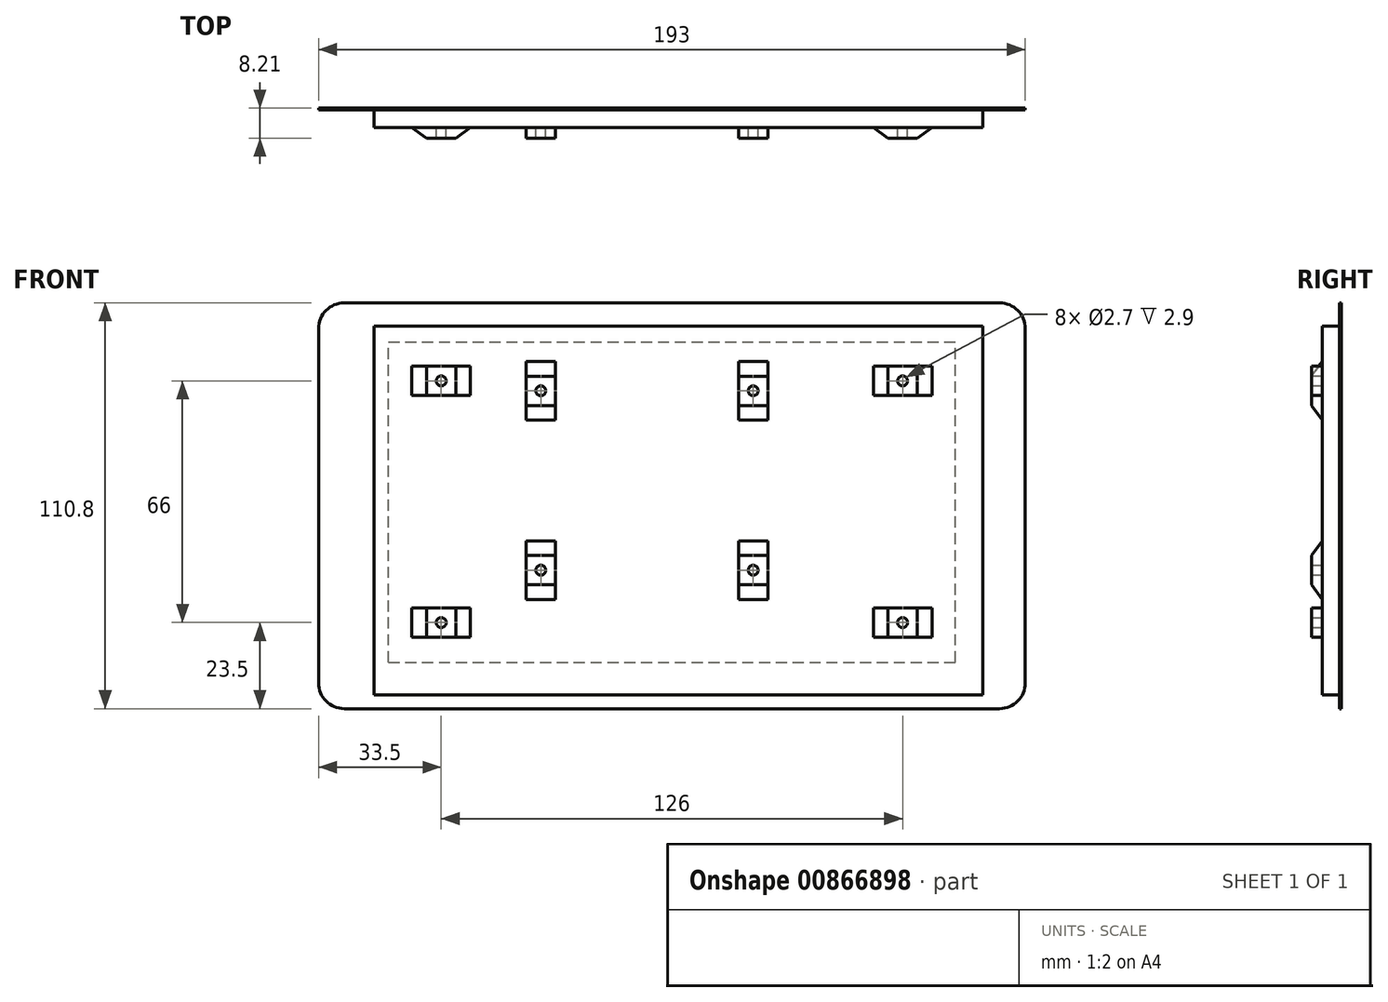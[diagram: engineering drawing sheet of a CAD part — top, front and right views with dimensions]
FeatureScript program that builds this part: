
annotation { "Feature Type Name" : "Feature", "Feature Type Description" : "" }
export const myFeature = defineFeature(function(context is Context, id is Id, definition is map)
    precondition{}
    {
        {
            var Q0;
            Q0=qCreatedBy(makeId("Front.planeOp"),FACE);
            var sketch = newSketch(context, id + "F0", { "sketchPlane" : qUnion([Q0])});
            skLineSegment(sketch, "E0.bottom", {"start": v(-111.7, 73) * mm, "end": v(67.3, 73) * mm});
            skLineSegment(sketch, "E0.top", {"start": v(-111.7, -37.8) * mm, "end": v(67.3, -37.8) * mm});
            skLineSegment(sketch, "E0.left", {"start": v(-118.7, 66) * mm, "end": v(-118.7, -30.8) * mm});
            skLineSegment(sketch, "E0.right", {"start": v(74.3, 66) * mm, "end": v(74.3, -30.8) * mm});
            skPoint(sketch, "E1.visualSharp", {"position": v(-118.7, 73) * mm});
            skArc(sketch, "E1.filletArc", {"start": v(-111.7, 73) * mm, "mid": v(-116.65, 70.95) * mm, "end": v(-118.7, 66) * mm});
            skPoint(sketch, "E2.visualSharp", {"position": v(-118.7, -37.8) * mm});
            skArc(sketch, "E2.filletArc", {"start": v(-118.7, -30.8) * mm, "mid": v(-116.65, -35.75) * mm, "end": v(-111.7, -37.8) * mm});
            skPoint(sketch, "E3.visualSharp", {"position": v(74.3, -37.8) * mm});
            skArc(sketch, "E3.filletArc", {"start": v(67.3, -37.8) * mm, "mid": v(72.25, -35.75) * mm, "end": v(74.3, -30.8) * mm});
            skPoint(sketch, "E4.visualSharp", {"position": v(74.3, 73) * mm});
            skArc(sketch, "E4.filletArc", {"start": v(74.3, 66) * mm, "mid": v(72.25, 70.95) * mm, "end": v(67.3, 73) * mm});
            skCircle(sketch, "E5", {"center": v(-58, 49) * mm, "radius": 1.35 * mm});
            skCircle(sketch, "E6", {"center": v(0, 49) * mm, "radius": 1.35 * mm});
            skCircle(sketch, "E7", {"center": v(-58, 0) * mm, "radius": 1.35 * mm});
            skCircle(sketch, "E8", {"center": v(0, 0) * mm, "radius": 1.35 * mm});
            skCircle(sketch, "E9", {"center": v(-85.2, 51.7) * mm, "radius": 1.35 * mm});
            skCircle(sketch, "E10", {"center": v(40.8, 51.7) * mm, "radius": 1.35 * mm});
            skCircle(sketch, "E11", {"center": v(40.8, -14.3) * mm, "radius": 1.35 * mm});
            skCircle(sketch, "E12", {"center": v(-85.2, -14.3) * mm, "radius": 1.35 * mm});
            skLineSegment(sketch, "E13", {"start": v(-85.2, -14.3) * mm, "end": v(-118.7, -14.3) * mm, "construction": true});
            skLineSegment(sketch, "E14", {"start": v(40.8, -14.3) * mm, "end": v(74.3, -14.3) * mm, "construction": true});
            skLineSegment(sketch, "E15.bottom", {"start": v(-103.6, 66.7) * mm, "end": v(62.7, 66.7) * mm});
            skLineSegment(sketch, "E15.top", {"start": v(-103.6, -34) * mm, "end": v(62.7, -34) * mm});
            skLineSegment(sketch, "E15.left", {"start": v(-103.6, 66.7) * mm, "end": v(-103.6, -34) * mm});
            skLineSegment(sketch, "E15.right", {"start": v(62.7, 66.7) * mm, "end": v(62.7, -34) * mm});
            skLineSegment(sketch, "E16.bottom", {"start": v(-54, 45) * mm, "end": v(-62, 45) * mm});
            skLineSegment(sketch, "E16.top", {"start": v(-54, 53) * mm, "end": v(-62, 53) * mm});
            skLineSegment(sketch, "E16.left", {"start": v(-54, 45) * mm, "end": v(-54, 53) * mm});
            skLineSegment(sketch, "E16.right", {"start": v(-62, 45) * mm, "end": v(-62, 53) * mm});
            skLineSegment(sketch, "E17.bottom", {"start": v(4, 45) * mm, "end": v(-4, 45) * mm});
            skLineSegment(sketch, "E17.top", {"start": v(4, 53) * mm, "end": v(-4, 53) * mm});
            skLineSegment(sketch, "E17.left", {"start": v(4, 45) * mm, "end": v(4, 53) * mm});
            skLineSegment(sketch, "E17.right", {"start": v(-4, 45) * mm, "end": v(-4, 53) * mm});
            skLineSegment(sketch, "E18.bottom", {"start": v(4, -4) * mm, "end": v(-4, -4) * mm});
            skLineSegment(sketch, "E18.top", {"start": v(4, 4) * mm, "end": v(-4, 4) * mm});
            skLineSegment(sketch, "E18.left", {"start": v(4, -4) * mm, "end": v(4, 4) * mm});
            skLineSegment(sketch, "E18.right", {"start": v(-4, -4) * mm, "end": v(-4, 4) * mm});
            skLineSegment(sketch, "E19.bottom", {"start": v(-54, -4) * mm, "end": v(-62, -4) * mm});
            skLineSegment(sketch, "E19.top", {"start": v(-54, 4) * mm, "end": v(-62, 4) * mm});
            skLineSegment(sketch, "E19.left", {"start": v(-54, -4) * mm, "end": v(-54, 4) * mm});
            skLineSegment(sketch, "E19.right", {"start": v(-62, -4) * mm, "end": v(-62, 4) * mm});
            skLineSegment(sketch, "E20.bottom", {"start": v(-81.2, -18.3) * mm, "end": v(-89.2, -18.3) * mm});
            skLineSegment(sketch, "E20.top", {"start": v(-81.2, -10.3) * mm, "end": v(-89.2, -10.3) * mm});
            skLineSegment(sketch, "E20.left", {"start": v(-81.2, -18.3) * mm, "end": v(-81.2, -10.3) * mm});
            skLineSegment(sketch, "E20.right", {"start": v(-89.2, -18.3) * mm, "end": v(-89.2, -10.3) * mm});
            skLineSegment(sketch, "E21.bottom", {"start": v(-81.2, 47.7) * mm, "end": v(-89.2, 47.7) * mm});
            skLineSegment(sketch, "E21.top", {"start": v(-81.2, 55.7) * mm, "end": v(-89.2, 55.7) * mm});
            skLineSegment(sketch, "E21.left", {"start": v(-81.2, 47.7) * mm, "end": v(-81.2, 55.7) * mm});
            skLineSegment(sketch, "E21.right", {"start": v(-89.2, 47.7) * mm, "end": v(-89.2, 55.7) * mm});
            skLineSegment(sketch, "E22.bottom", {"start": v(44.8, 47.7) * mm, "end": v(36.8, 47.7) * mm});
            skLineSegment(sketch, "E22.top", {"start": v(44.8, 55.7) * mm, "end": v(36.8, 55.7) * mm});
            skLineSegment(sketch, "E22.left", {"start": v(44.8, 47.7) * mm, "end": v(44.8, 55.7) * mm});
            skLineSegment(sketch, "E22.right", {"start": v(36.8, 47.7) * mm, "end": v(36.8, 55.7) * mm});
            skLineSegment(sketch, "E23.bottom", {"start": v(44.8, -18.3) * mm, "end": v(36.8, -18.3) * mm});
            skLineSegment(sketch, "E23.top", {"start": v(44.8, -10.3) * mm, "end": v(36.8, -10.3) * mm});
            skLineSegment(sketch, "E23.left", {"start": v(44.8, -18.3) * mm, "end": v(44.8, -10.3) * mm});
            skLineSegment(sketch, "E23.right", {"start": v(36.8, -18.3) * mm, "end": v(36.8, -10.3) * mm});
            skLineSegment(sketch, "E24.bottom", {"start": v(-99.6, -25.1) * mm, "end": v(55.2, -25.1) * mm});
            skLineSegment(sketch, "E24.top", {"start": v(-99.6, 62.3) * mm, "end": v(55.2, 62.3) * mm});
            skLineSegment(sketch, "E24.left", {"start": v(-99.6, -25.1) * mm, "end": v(-99.6, 62.3) * mm});
            skLineSegment(sketch, "E24.right", {"start": v(55.2, -25.1) * mm, "end": v(55.2, 62.3) * mm});
            skPoint(sketch, "E24.middle", {"position": v(-22.2, 18.6) * mm});
            skLineSegment(sketch, "E25", {"start": v(55.2, 18.6) * mm, "end": v(74.3, 18.6) * mm, "construction": true});
            skPoint(sketch, "E25.endSnap0", {"position": v(74.3, 17.6) * mm});
            skLineSegment(sketch, "E26", {"start": v(-99.6, 18.6) * mm, "end": v(-118.7, 18.6) * mm, "construction": true});
            skSolve(sketch);
        }
        {
            var Q0;
            Q0=makeQuery(id+"F0.imprint","IMPRINT",FACE,{"disambiguationData":[TD([[makeQuery(id+"F0.imprint","IMPRINT",EDGE,{"derivedFrom":sQuery(id+"F0.wireOp",EDGE,"E15.bottom")}),-1.0]])]});
            var Q1;
            Q1=makeQuery(id+"F0.imprint","IMPRINT",FACE,{"disambiguationData":[TD([[makeQuery(id+"F0.imprint","IMPRINT",EDGE,{"derivedFrom":sQuery(id+"F0.wireOp",EDGE,"E5")}),-1.0]])]});
            var Q2;
            Q2=makeQuery(id+"F0.imprint","IMPRINT",FACE,{"disambiguationData":[TD([[makeQuery(id+"F0.imprint","IMPRINT",EDGE,{"derivedFrom":sQuery(id+"F0.wireOp",EDGE,"E9")}),-1.0]])]});
            var Q3;
            Q3=makeQuery(id+"F0.imprint","IMPRINT",FACE,{"disambiguationData":[TD([[makeQuery(id+"F0.imprint","IMPRINT",EDGE,{"derivedFrom":sQuery(id+"F0.wireOp",EDGE,"E6")}),1.0]])]});
            var Q4;
            Q4=makeQuery(id+"F0.imprint","IMPRINT",FACE,{"disambiguationData":[TD([[makeQuery(id+"F0.imprint","IMPRINT",EDGE,{"derivedFrom":sQuery(id+"F0.wireOp",EDGE,"E10")}),-1.0]])]});
            var Q5;
            Q5=makeQuery(id+"F0.imprint","IMPRINT",FACE,{"disambiguationData":[TD([[makeQuery(id+"F0.imprint","IMPRINT",EDGE,{"derivedFrom":sQuery(id+"F0.wireOp",EDGE,"E8")}),-1.0]])]});
            var Q6;
            Q6=makeQuery(id+"F0.imprint","IMPRINT",FACE,{"disambiguationData":[TD([[makeQuery(id+"F0.imprint","IMPRINT",EDGE,{"derivedFrom":sQuery(id+"F0.wireOp",EDGE,"E11")}),-1.0]])]});
            var Q7;
            Q7=makeQuery(id+"F0.imprint","IMPRINT",FACE,{"disambiguationData":[TD([[makeQuery(id+"F0.imprint","IMPRINT",EDGE,{"derivedFrom":sQuery(id+"F0.wireOp",EDGE,"E6")}),-1.0]])]});
            var Q8;
            Q8=makeQuery(id+"F0.imprint","IMPRINT",FACE,{"disambiguationData":[TD([[makeQuery(id+"F0.imprint","IMPRINT",EDGE,{"derivedFrom":sQuery(id+"F0.wireOp",EDGE,"E10")}),1.0]])]});
            var Q9;
            Q9=makeQuery(id+"F0.imprint","IMPRINT",FACE,{"disambiguationData":[TD([[makeQuery(id+"F0.imprint","IMPRINT",EDGE,{"derivedFrom":sQuery(id+"F0.wireOp",EDGE,"E11")}),1.0]])]});
            var Q10;
            Q10=makeQuery(id+"F0.imprint","IMPRINT",FACE,{"disambiguationData":[TD([[makeQuery(id+"F0.imprint","IMPRINT",EDGE,{"derivedFrom":sQuery(id+"F0.wireOp",EDGE,"E8")}),1.0]])]});
            var Q11;
            Q11=makeQuery(id+"F0.imprint","IMPRINT",FACE,{"disambiguationData":[TD([[makeQuery(id+"F0.imprint","IMPRINT",EDGE,{"derivedFrom":sQuery(id+"F0.wireOp",EDGE,"E5")}),1.0]])]});
            var Q12;
            Q12=makeQuery(id+"F0.imprint","IMPRINT",FACE,{"disambiguationData":[TD([[makeQuery(id+"F0.imprint","IMPRINT",EDGE,{"derivedFrom":sQuery(id+"F0.wireOp",EDGE,"E7")}),1.0]])]});
            var Q13;
            Q13=makeQuery(id+"F0.imprint","IMPRINT",FACE,{"disambiguationData":[TD([[makeQuery(id+"F0.imprint","IMPRINT",EDGE,{"derivedFrom":sQuery(id+"F0.wireOp",EDGE,"E7")}),-1.0]])]});
            var Q14;
            Q14=makeQuery(id+"F0.imprint","IMPRINT",FACE,{"disambiguationData":[TD([[makeQuery(id+"F0.imprint","IMPRINT",EDGE,{"derivedFrom":sQuery(id+"F0.wireOp",EDGE,"E9")}),1.0]])]});
            var Q15;
            Q15=makeQuery(id+"F0.imprint","IMPRINT",FACE,{"disambiguationData":[TD([[makeQuery(id+"F0.imprint","IMPRINT",EDGE,{"derivedFrom":sQuery(id+"F0.wireOp",EDGE,"E12")}),1.0]])]});
            var Q16;
            Q16=makeQuery(id+"F0.imprint","IMPRINT",FACE,{"disambiguationData":[TD([[makeQuery(id+"F0.imprint","IMPRINT",EDGE,{"derivedFrom":sQuery(id+"F0.wireOp",EDGE,"E12")}),-1.0]])]});
            var Q17;
            Q17=makeQuery(id+"F0.imprint","IMPRINT",FACE,{"disambiguationData":[TD([[makeQuery(id+"F0.imprint","IMPRINT",EDGE,{"derivedFrom":sQuery(id+"F0.wireOp",EDGE,"E0.bottom")}),-1.0]])]});
            var Q18;
            Q18=makeQuery(id+"F0.imprint","IMPRINT",FACE,{"disambiguationData":[TD([[makeQuery(id+"F0.imprint","IMPRINT",EDGE,{"derivedFrom":sQuery(id+"F0.wireOp",EDGE,"E16.bottom")}),1.0]])]});
            var Q19;
            Q19=sQuery(id+"F0.wireOp",EDGE,"E0.bottom");
            var Q20;
            Q20=sQuery(id+"F0.wireOp",EDGE,"E1.filletArc");
            var Q21;
            Q21=sQuery(id+"F0.wireOp",EDGE,"E0.left");
            var Q22;
            Q22=sQuery(id+"F0.wireOp",EDGE,"E2.filletArc");
            var Q23;
            Q23=sQuery(id+"F0.wireOp",EDGE,"E0.top");
            var Q24;
            Q24=sQuery(id+"F0.wireOp",EDGE,"E3.filletArc");
            var Q25;
            Q25=sQuery(id+"F0.wireOp",EDGE,"E0.right");
            var Q26;
            Q26=sQuery(id+"F0.wireOp",EDGE,"E4.filletArc");
            extrude(context, id + "F1", {"entities" : qUnion([Q0, Q1, Q2, Q3, Q4, Q5, Q6, Q7, Q8, Q9, Q10, Q11, Q12, Q13, Q14, Q15, Q16, Q17, Q18]), "surfaceEntities" : qUnion([Q19, Q20, Q21, Q22, Q23, Q24, Q25, Q26]), "oppositeDirection" : true, "depth" : .5 * mm, "offsetDistance" : 25 * mm});
        }
        {
            var Q0;
            Q0=makeQuery(id+"F0.imprint","IMPRINT",FACE,{"disambiguationData":[TD([[makeQuery(id+"F0.imprint","IMPRINT",EDGE,{"derivedFrom":sQuery(id+"F0.wireOp",EDGE,"E15.bottom")}),-1.0]])]});
            var Q1;
            Q1=makeQuery(id+"F0.imprint","IMPRINT",FACE,{"disambiguationData":[TD([[makeQuery(id+"F0.imprint","IMPRINT",EDGE,{"derivedFrom":sQuery(id+"F0.wireOp",EDGE,"E10")}),-1.0]])]});
            var Q2;
            Q2=makeQuery(id+"F0.imprint","IMPRINT",FACE,{"disambiguationData":[TD([[makeQuery(id+"F0.imprint","IMPRINT",EDGE,{"derivedFrom":sQuery(id+"F0.wireOp",EDGE,"E10")}),1.0]])]});
            var Q3;
            Q3=makeQuery(id+"F0.imprint","IMPRINT",FACE,{"disambiguationData":[TD([[makeQuery(id+"F0.imprint","IMPRINT",EDGE,{"derivedFrom":sQuery(id+"F0.wireOp",EDGE,"E6")}),-1.0]])]});
            var Q4;
            Q4=makeQuery(id+"F0.imprint","IMPRINT",FACE,{"disambiguationData":[TD([[makeQuery(id+"F0.imprint","IMPRINT",EDGE,{"derivedFrom":sQuery(id+"F0.wireOp",EDGE,"E6")}),1.0]])]});
            var Q5;
            Q5=makeQuery(id+"F0.imprint","IMPRINT",FACE,{"disambiguationData":[TD([[makeQuery(id+"F0.imprint","IMPRINT",EDGE,{"derivedFrom":sQuery(id+"F0.wireOp",EDGE,"E5")}),-1.0]])]});
            var Q6;
            Q6=makeQuery(id+"F0.imprint","IMPRINT",FACE,{"disambiguationData":[TD([[makeQuery(id+"F0.imprint","IMPRINT",EDGE,{"derivedFrom":sQuery(id+"F0.wireOp",EDGE,"E5")}),1.0]])]});
            var Q7;
            Q7=makeQuery(id+"F0.imprint","IMPRINT",FACE,{"disambiguationData":[TD([[makeQuery(id+"F0.imprint","IMPRINT",EDGE,{"derivedFrom":sQuery(id+"F0.wireOp",EDGE,"E9")}),-1.0]])]});
            var Q8;
            Q8=makeQuery(id+"F0.imprint","IMPRINT",FACE,{"disambiguationData":[TD([[makeQuery(id+"F0.imprint","IMPRINT",EDGE,{"derivedFrom":sQuery(id+"F0.wireOp",EDGE,"E9")}),1.0]])]});
            var Q9;
            Q9=makeQuery(id+"F0.imprint","IMPRINT",FACE,{"disambiguationData":[TD([[makeQuery(id+"F0.imprint","IMPRINT",EDGE,{"derivedFrom":sQuery(id+"F0.wireOp",EDGE,"E7")}),-1.0]])]});
            var Q10;
            Q10=makeQuery(id+"F0.imprint","IMPRINT",FACE,{"disambiguationData":[TD([[makeQuery(id+"F0.imprint","IMPRINT",EDGE,{"derivedFrom":sQuery(id+"F0.wireOp",EDGE,"E7")}),1.0]])]});
            var Q11;
            Q11=makeQuery(id+"F0.imprint","IMPRINT",FACE,{"disambiguationData":[TD([[makeQuery(id+"F0.imprint","IMPRINT",EDGE,{"derivedFrom":sQuery(id+"F0.wireOp",EDGE,"E12")}),-1.0]])]});
            var Q12;
            Q12=makeQuery(id+"F0.imprint","IMPRINT",FACE,{"disambiguationData":[TD([[makeQuery(id+"F0.imprint","IMPRINT",EDGE,{"derivedFrom":sQuery(id+"F0.wireOp",EDGE,"E12")}),1.0]])]});
            var Q13;
            Q13=makeQuery(id+"F0.imprint","IMPRINT",FACE,{"disambiguationData":[TD([[makeQuery(id+"F0.imprint","IMPRINT",EDGE,{"derivedFrom":sQuery(id+"F0.wireOp",EDGE,"E8")}),-1.0]])]});
            var Q14;
            Q14=makeQuery(id+"F0.imprint","IMPRINT",FACE,{"disambiguationData":[TD([[makeQuery(id+"F0.imprint","IMPRINT",EDGE,{"derivedFrom":sQuery(id+"F0.wireOp",EDGE,"E8")}),1.0]])]});
            var Q15;
            Q15=makeQuery(id+"F0.imprint","IMPRINT",FACE,{"disambiguationData":[TD([[makeQuery(id+"F0.imprint","IMPRINT",EDGE,{"derivedFrom":sQuery(id+"F0.wireOp",EDGE,"E11")}),-1.0]])]});
            var Q16;
            Q16=makeQuery(id+"F0.imprint","IMPRINT",FACE,{"disambiguationData":[TD([[makeQuery(id+"F0.imprint","IMPRINT",EDGE,{"derivedFrom":sQuery(id+"F0.wireOp",EDGE,"E11")}),1.0]])]});
            var Q17;
            Q17=makeQuery(id+"F0.imprint","IMPRINT",FACE,{"disambiguationData":[TD([[makeQuery(id+"F0.imprint","IMPRINT",EDGE,{"derivedFrom":sQuery(id+"F0.wireOp",EDGE,"E16.bottom")}),1.0]])]});
            extrude(context, id + "F2", {"entities" : qUnion([Q0, Q1, Q2, Q3, Q4, Q5, Q6, Q7, Q8, Q9, Q10, Q11, Q12, Q13, Q14, Q15, Q16, Q17]), "depth" : 4.8 * mm, "offsetDistance" : 25 * mm});
        }
        {
            var Q0;
            Q0=makeQuery(id+"F0.imprint","IMPRINT",FACE,{"disambiguationData":[TD([[makeQuery(id+"F0.imprint","IMPRINT",EDGE,{"derivedFrom":sQuery(id+"F0.wireOp",EDGE,"E5")}),-1.0]])]});
            var Q1;
            Q1=makeQuery(id+"F0.imprint","IMPRINT",FACE,{"disambiguationData":[TD([[makeQuery(id+"F0.imprint","IMPRINT",EDGE,{"derivedFrom":sQuery(id+"F0.wireOp",EDGE,"E6")}),-1.0]])]});
            var Q2;
            Q2=makeQuery(id+"F0.imprint","IMPRINT",FACE,{"disambiguationData":[TD([[makeQuery(id+"F0.imprint","IMPRINT",EDGE,{"derivedFrom":sQuery(id+"F0.wireOp",EDGE,"E10")}),-1.0]])]});
            var Q3;
            Q3=makeQuery(id+"F0.imprint","IMPRINT",FACE,{"disambiguationData":[TD([[makeQuery(id+"F0.imprint","IMPRINT",EDGE,{"derivedFrom":sQuery(id+"F0.wireOp",EDGE,"E11")}),-1.0]])]});
            var Q4;
            Q4=makeQuery(id+"F0.imprint","IMPRINT",FACE,{"disambiguationData":[TD([[makeQuery(id+"F0.imprint","IMPRINT",EDGE,{"derivedFrom":sQuery(id+"F0.wireOp",EDGE,"E8")}),-1.0]])]});
            var Q5;
            Q5=makeQuery(id+"F0.imprint","IMPRINT",FACE,{"disambiguationData":[TD([[makeQuery(id+"F0.imprint","IMPRINT",EDGE,{"derivedFrom":sQuery(id+"F0.wireOp",EDGE,"E7")}),-1.0]])]});
            var Q6;
            Q6=makeQuery(id+"F0.imprint","IMPRINT",FACE,{"disambiguationData":[TD([[makeQuery(id+"F0.imprint","IMPRINT",EDGE,{"derivedFrom":sQuery(id+"F0.wireOp",EDGE,"E12")}),-1.0]])]});
            var Q7;
            Q7=makeQuery(id+"F0.imprint","IMPRINT",FACE,{"disambiguationData":[TD([[makeQuery(id+"F0.imprint","IMPRINT",EDGE,{"derivedFrom":sQuery(id+"F0.wireOp",EDGE,"E9")}),-1.0]])]});
            extrude(context, id + "F3", {"entities" : qUnion([Q0, Q1, Q2, Q3, Q4, Q5, Q6, Q7]), "operationType" : NewBodyOperationType.ADD, "depth" : 7.7 * mm, "offsetDistance" : 25 * mm});
        }
        {
            var Q0;
            Q0=makeQuery(id+"F3.boolean.opBoolean","INTERSECT",EDGE,{"derivedFrom":[makeQuery(id+"F2.opExtrude","CAP_FACE",FACE,{"disambiguationData":[OSD([sQuery(id+"F0.wireOp",EDGE,"E15.bottom"),sQuery(id+"F0.wireOp",EDGE,"E15.top"),sQuery(id+"F0.wireOp",EDGE,"E15.left"),sQuery(id+"F0.wireOp",EDGE,"E15.right")])],"isStart":false}),makeQuery(id+"F3.opExtrude","SWEPT_FACE",FACE,{"disambiguationData":[OSD([sQuery(id+"F0.wireOp",EDGE,"E16.top")])]})]});
            var Q1;
            Q1=makeQuery(id+"F3.boolean.opBoolean","INTERSECT",EDGE,{"derivedFrom":[makeQuery(id+"F2.opExtrude","CAP_FACE",FACE,{"disambiguationData":[OSD([sQuery(id+"F0.wireOp",EDGE,"E15.bottom"),sQuery(id+"F0.wireOp",EDGE,"E15.top"),sQuery(id+"F0.wireOp",EDGE,"E15.left"),sQuery(id+"F0.wireOp",EDGE,"E15.right")])],"isStart":false}),makeQuery(id+"F3.opExtrude","SWEPT_FACE",FACE,{"disambiguationData":[OSD([sQuery(id+"F0.wireOp",EDGE,"E16.bottom")])]})]});
            var Q2;
            Q2=makeQuery(id+"F3.boolean.opBoolean","INTERSECT",EDGE,{"derivedFrom":[makeQuery(id+"F2.opExtrude","CAP_FACE",FACE,{"disambiguationData":[OSD([sQuery(id+"F0.wireOp",EDGE,"E15.bottom"),sQuery(id+"F0.wireOp",EDGE,"E15.top"),sQuery(id+"F0.wireOp",EDGE,"E15.left"),sQuery(id+"F0.wireOp",EDGE,"E15.right")])],"isStart":false}),makeQuery(id+"F3.opExtrude","SWEPT_FACE",FACE,{"disambiguationData":[OSD([sQuery(id+"F0.wireOp",EDGE,"E21.right")])]})]});
            var Q3;
            Q3=makeQuery(id+"F3.boolean.opBoolean","INTERSECT",EDGE,{"derivedFrom":[makeQuery(id+"F2.opExtrude","CAP_FACE",FACE,{"disambiguationData":[OSD([sQuery(id+"F0.wireOp",EDGE,"E15.bottom"),sQuery(id+"F0.wireOp",EDGE,"E15.top"),sQuery(id+"F0.wireOp",EDGE,"E15.left"),sQuery(id+"F0.wireOp",EDGE,"E15.right")])],"isStart":false}),makeQuery(id+"F3.opExtrude","SWEPT_FACE",FACE,{"disambiguationData":[OSD([sQuery(id+"F0.wireOp",EDGE,"E21.left")])]})]});
            var Q4;
            Q4=makeQuery(id+"F3.boolean.opBoolean","INTERSECT",EDGE,{"derivedFrom":[makeQuery(id+"F2.opExtrude","CAP_FACE",FACE,{"disambiguationData":[OSD([sQuery(id+"F0.wireOp",EDGE,"E15.bottom"),sQuery(id+"F0.wireOp",EDGE,"E15.top"),sQuery(id+"F0.wireOp",EDGE,"E15.left"),sQuery(id+"F0.wireOp",EDGE,"E15.right")])],"isStart":false}),makeQuery(id+"F3.opExtrude","SWEPT_FACE",FACE,{"disambiguationData":[OSD([sQuery(id+"F0.wireOp",EDGE,"E17.bottom")])]})]});
            var Q5;
            Q5=makeQuery(id+"F3.boolean.opBoolean","INTERSECT",EDGE,{"derivedFrom":[makeQuery(id+"F2.opExtrude","CAP_FACE",FACE,{"disambiguationData":[OSD([sQuery(id+"F0.wireOp",EDGE,"E15.bottom"),sQuery(id+"F0.wireOp",EDGE,"E15.top"),sQuery(id+"F0.wireOp",EDGE,"E15.left"),sQuery(id+"F0.wireOp",EDGE,"E15.right")])],"isStart":false}),makeQuery(id+"F3.opExtrude","SWEPT_FACE",FACE,{"disambiguationData":[OSD([sQuery(id+"F0.wireOp",EDGE,"E18.bottom")])]})]});
            var Q6;
            Q6=makeQuery(id+"F3.boolean.opBoolean","INTERSECT",EDGE,{"derivedFrom":[makeQuery(id+"F2.opExtrude","CAP_FACE",FACE,{"disambiguationData":[OSD([sQuery(id+"F0.wireOp",EDGE,"E15.bottom"),sQuery(id+"F0.wireOp",EDGE,"E15.top"),sQuery(id+"F0.wireOp",EDGE,"E15.left"),sQuery(id+"F0.wireOp",EDGE,"E15.right")])],"isStart":false}),makeQuery(id+"F3.opExtrude","SWEPT_FACE",FACE,{"disambiguationData":[OSD([sQuery(id+"F0.wireOp",EDGE,"E23.left")])]})]});
            var Q7;
            Q7=makeQuery(id+"F3.boolean.opBoolean","INTERSECT",EDGE,{"derivedFrom":[makeQuery(id+"F2.opExtrude","CAP_FACE",FACE,{"disambiguationData":[OSD([sQuery(id+"F0.wireOp",EDGE,"E15.bottom"),sQuery(id+"F0.wireOp",EDGE,"E15.top"),sQuery(id+"F0.wireOp",EDGE,"E15.left"),sQuery(id+"F0.wireOp",EDGE,"E15.right")])],"isStart":false}),makeQuery(id+"F3.opExtrude","SWEPT_FACE",FACE,{"disambiguationData":[OSD([sQuery(id+"F0.wireOp",EDGE,"E22.left")])]})]});
            var Q8;
            Q8=makeQuery(id+"F3.boolean.opBoolean","INTERSECT",EDGE,{"derivedFrom":[makeQuery(id+"F2.opExtrude","CAP_FACE",FACE,{"disambiguationData":[OSD([sQuery(id+"F0.wireOp",EDGE,"E15.bottom"),sQuery(id+"F0.wireOp",EDGE,"E15.top"),sQuery(id+"F0.wireOp",EDGE,"E15.left"),sQuery(id+"F0.wireOp",EDGE,"E15.right")])],"isStart":false}),makeQuery(id+"F3.opExtrude","SWEPT_FACE",FACE,{"disambiguationData":[OSD([sQuery(id+"F0.wireOp",EDGE,"E19.bottom")])]})]});
            var Q9;
            Q9=makeQuery(id+"F3.boolean.opBoolean","INTERSECT",EDGE,{"derivedFrom":[makeQuery(id+"F2.opExtrude","CAP_FACE",FACE,{"disambiguationData":[OSD([sQuery(id+"F0.wireOp",EDGE,"E15.bottom"),sQuery(id+"F0.wireOp",EDGE,"E15.top"),sQuery(id+"F0.wireOp",EDGE,"E15.left"),sQuery(id+"F0.wireOp",EDGE,"E15.right")])],"isStart":false}),makeQuery(id+"F3.opExtrude","SWEPT_FACE",FACE,{"disambiguationData":[OSD([sQuery(id+"F0.wireOp",EDGE,"E20.left")])]})]});
            var Q10;
            Q10=makeQuery(id+"F3.boolean.opBoolean","INTERSECT",EDGE,{"derivedFrom":[makeQuery(id+"F2.opExtrude","CAP_FACE",FACE,{"disambiguationData":[OSD([sQuery(id+"F0.wireOp",EDGE,"E15.bottom"),sQuery(id+"F0.wireOp",EDGE,"E15.top"),sQuery(id+"F0.wireOp",EDGE,"E15.left"),sQuery(id+"F0.wireOp",EDGE,"E15.right")])],"isStart":false}),makeQuery(id+"F3.opExtrude","SWEPT_FACE",FACE,{"disambiguationData":[OSD([sQuery(id+"F0.wireOp",EDGE,"E20.right")])]})]});
            var Q11;
            Q11=makeQuery(id+"F3.boolean.opBoolean","INTERSECT",EDGE,{"derivedFrom":[makeQuery(id+"F2.opExtrude","CAP_FACE",FACE,{"disambiguationData":[OSD([sQuery(id+"F0.wireOp",EDGE,"E15.bottom"),sQuery(id+"F0.wireOp",EDGE,"E15.top"),sQuery(id+"F0.wireOp",EDGE,"E15.left"),sQuery(id+"F0.wireOp",EDGE,"E15.right")])],"isStart":false}),makeQuery(id+"F3.opExtrude","SWEPT_FACE",FACE,{"disambiguationData":[OSD([sQuery(id+"F0.wireOp",EDGE,"E22.right")])]})]});
            var Q12;
            Q12=makeQuery(id+"F3.boolean.opBoolean","INTERSECT",EDGE,{"derivedFrom":[makeQuery(id+"F2.opExtrude","CAP_FACE",FACE,{"disambiguationData":[OSD([sQuery(id+"F0.wireOp",EDGE,"E15.bottom"),sQuery(id+"F0.wireOp",EDGE,"E15.top"),sQuery(id+"F0.wireOp",EDGE,"E15.left"),sQuery(id+"F0.wireOp",EDGE,"E15.right")])],"isStart":false}),makeQuery(id+"F3.opExtrude","SWEPT_FACE",FACE,{"disambiguationData":[OSD([sQuery(id+"F0.wireOp",EDGE,"E23.right")])]})]});
            var Q13;
            Q13=makeQuery(id+"F3.boolean.opBoolean","INTERSECT",EDGE,{"derivedFrom":[makeQuery(id+"F2.opExtrude","CAP_FACE",FACE,{"disambiguationData":[OSD([sQuery(id+"F0.wireOp",EDGE,"E15.bottom"),sQuery(id+"F0.wireOp",EDGE,"E15.top"),sQuery(id+"F0.wireOp",EDGE,"E15.left"),sQuery(id+"F0.wireOp",EDGE,"E15.right")])],"isStart":false}),makeQuery(id+"F3.opExtrude","SWEPT_FACE",FACE,{"disambiguationData":[OSD([sQuery(id+"F0.wireOp",EDGE,"E17.top")])]})]});
            var Q14;
            Q14=makeQuery(id+"F3.boolean.opBoolean","INTERSECT",EDGE,{"derivedFrom":[makeQuery(id+"F2.opExtrude","CAP_FACE",FACE,{"disambiguationData":[OSD([sQuery(id+"F0.wireOp",EDGE,"E15.bottom"),sQuery(id+"F0.wireOp",EDGE,"E15.top"),sQuery(id+"F0.wireOp",EDGE,"E15.left"),sQuery(id+"F0.wireOp",EDGE,"E15.right")])],"isStart":false}),makeQuery(id+"F3.opExtrude","SWEPT_FACE",FACE,{"disambiguationData":[OSD([sQuery(id+"F0.wireOp",EDGE,"E18.top")])]})]});
            var Q15;
            Q15=makeQuery(id+"F3.boolean.opBoolean","INTERSECT",EDGE,{"derivedFrom":[makeQuery(id+"F2.opExtrude","CAP_FACE",FACE,{"disambiguationData":[OSD([sQuery(id+"F0.wireOp",EDGE,"E15.bottom"),sQuery(id+"F0.wireOp",EDGE,"E15.top"),sQuery(id+"F0.wireOp",EDGE,"E15.left"),sQuery(id+"F0.wireOp",EDGE,"E15.right")])],"isStart":false}),makeQuery(id+"F3.opExtrude","SWEPT_FACE",FACE,{"disambiguationData":[OSD([sQuery(id+"F0.wireOp",EDGE,"E19.top")])]})]});
            chamfer(context, id + "F4", {"entities" : qUnion([Q0, Q1, Q2, Q3, Q4, Q5, Q6, Q7, Q8, Q9, Q10, Q11, Q12, Q13, Q14, Q15]), "chamferType" : ChamferType.TWO_OFFSETS, "width1" : 4 * mm, "oppositeDirection" : false, "width2" : 2.9 * mm, "tangentPropagation" : true});
        }
        {
            var Q0;
            Q0=makeQuery(id+"F0.imprint","IMPRINT",FACE,{"disambiguationData":[TD([[makeQuery(id+"F0.imprint","IMPRINT",EDGE,{"derivedFrom":sQuery(id+"F0.wireOp",EDGE,"E10")}),-1.0]])]});
            var Q1;
            Q1=makeQuery(id+"F0.imprint","IMPRINT",FACE,{"disambiguationData":[TD([[makeQuery(id+"F0.imprint","IMPRINT",EDGE,{"derivedFrom":sQuery(id+"F0.wireOp",EDGE,"E10")}),1.0]])]});
            var Q2;
            Q2=makeQuery(id+"F0.imprint","IMPRINT",FACE,{"disambiguationData":[TD([[makeQuery(id+"F0.imprint","IMPRINT",EDGE,{"derivedFrom":sQuery(id+"F0.wireOp",EDGE,"E11")}),-1.0]])]});
            var Q3;
            Q3=makeQuery(id+"F0.imprint","IMPRINT",FACE,{"disambiguationData":[TD([[makeQuery(id+"F0.imprint","IMPRINT",EDGE,{"derivedFrom":sQuery(id+"F0.wireOp",EDGE,"E11")}),1.0]])]});
            var Q4;
            Q4=makeQuery(id+"F0.imprint","IMPRINT",FACE,{"disambiguationData":[TD([[makeQuery(id+"F0.imprint","IMPRINT",EDGE,{"derivedFrom":sQuery(id+"F0.wireOp",EDGE,"E6")}),-1.0]])]});
            var Q5;
            Q5=makeQuery(id+"F0.imprint","IMPRINT",FACE,{"disambiguationData":[TD([[makeQuery(id+"F0.imprint","IMPRINT",EDGE,{"derivedFrom":sQuery(id+"F0.wireOp",EDGE,"E5")}),-1.0]])]});
            var Q6;
            Q6=makeQuery(id+"F0.imprint","IMPRINT",FACE,{"disambiguationData":[TD([[makeQuery(id+"F0.imprint","IMPRINT",EDGE,{"derivedFrom":sQuery(id+"F0.wireOp",EDGE,"E9")}),-1.0]])]});
            var Q7;
            Q7=makeQuery(id+"F0.imprint","IMPRINT",FACE,{"disambiguationData":[TD([[makeQuery(id+"F0.imprint","IMPRINT",EDGE,{"derivedFrom":sQuery(id+"F0.wireOp",EDGE,"E7")}),-1.0]])]});
            var Q8;
            Q8=makeQuery(id+"F0.imprint","IMPRINT",FACE,{"disambiguationData":[TD([[makeQuery(id+"F0.imprint","IMPRINT",EDGE,{"derivedFrom":sQuery(id+"F0.wireOp",EDGE,"E8")}),1.0]])]});
            var Q9;
            Q9=makeQuery(id+"F0.imprint","IMPRINT",FACE,{"disambiguationData":[TD([[makeQuery(id+"F0.imprint","IMPRINT",EDGE,{"derivedFrom":sQuery(id+"F0.wireOp",EDGE,"E6")}),1.0]])]});
            var Q10;
            Q10=makeQuery(id+"F0.imprint","IMPRINT",FACE,{"disambiguationData":[TD([[makeQuery(id+"F0.imprint","IMPRINT",EDGE,{"derivedFrom":sQuery(id+"F0.wireOp",EDGE,"E5")}),1.0]])]});
            var Q11;
            Q11=makeQuery(id+"F0.imprint","IMPRINT",FACE,{"disambiguationData":[TD([[makeQuery(id+"F0.imprint","IMPRINT",EDGE,{"derivedFrom":sQuery(id+"F0.wireOp",EDGE,"E7")}),1.0]])]});
            var Q12;
            Q12=makeQuery(id+"F0.imprint","IMPRINT",FACE,{"disambiguationData":[TD([[makeQuery(id+"F0.imprint","IMPRINT",EDGE,{"derivedFrom":sQuery(id+"F0.wireOp",EDGE,"E9")}),1.0]])]});
            var Q13;
            Q13=makeQuery(id+"F0.imprint","IMPRINT",FACE,{"disambiguationData":[TD([[makeQuery(id+"F0.imprint","IMPRINT",EDGE,{"derivedFrom":sQuery(id+"F0.wireOp",EDGE,"E12")}),-1.0]])]});
            var Q14;
            Q14=makeQuery(id+"F0.imprint","IMPRINT",FACE,{"disambiguationData":[TD([[makeQuery(id+"F0.imprint","IMPRINT",EDGE,{"derivedFrom":sQuery(id+"F0.wireOp",EDGE,"E12")}),1.0]])]});
            var Q15;
            Q15=makeQuery(id+"F0.imprint","IMPRINT",FACE,{"disambiguationData":[TD([[makeQuery(id+"F0.imprint","IMPRINT",EDGE,{"derivedFrom":sQuery(id+"F0.wireOp",EDGE,"E8")}),-1.0]])]});
            var Q16;
            Q16=makeQuery(id+"F0.imprint","IMPRINT",FACE,{"disambiguationData":[TD([[makeQuery(id+"F0.imprint","IMPRINT",EDGE,{"derivedFrom":sQuery(id+"F0.wireOp",EDGE,"E16.bottom")}),1.0]])]});
            extrude(context, id + "F5", {"entities" : qUnion([Q0, Q1, Q2, Q3, Q4, Q5, Q6, Q7, Q8, Q9, Q10, Q11, Q12, Q13, Q14, Q15, Q16]), "oppositeDirection" : true, "depth" : .51 * mm, "offsetDistance" : 25 * mm});
        }
    });
